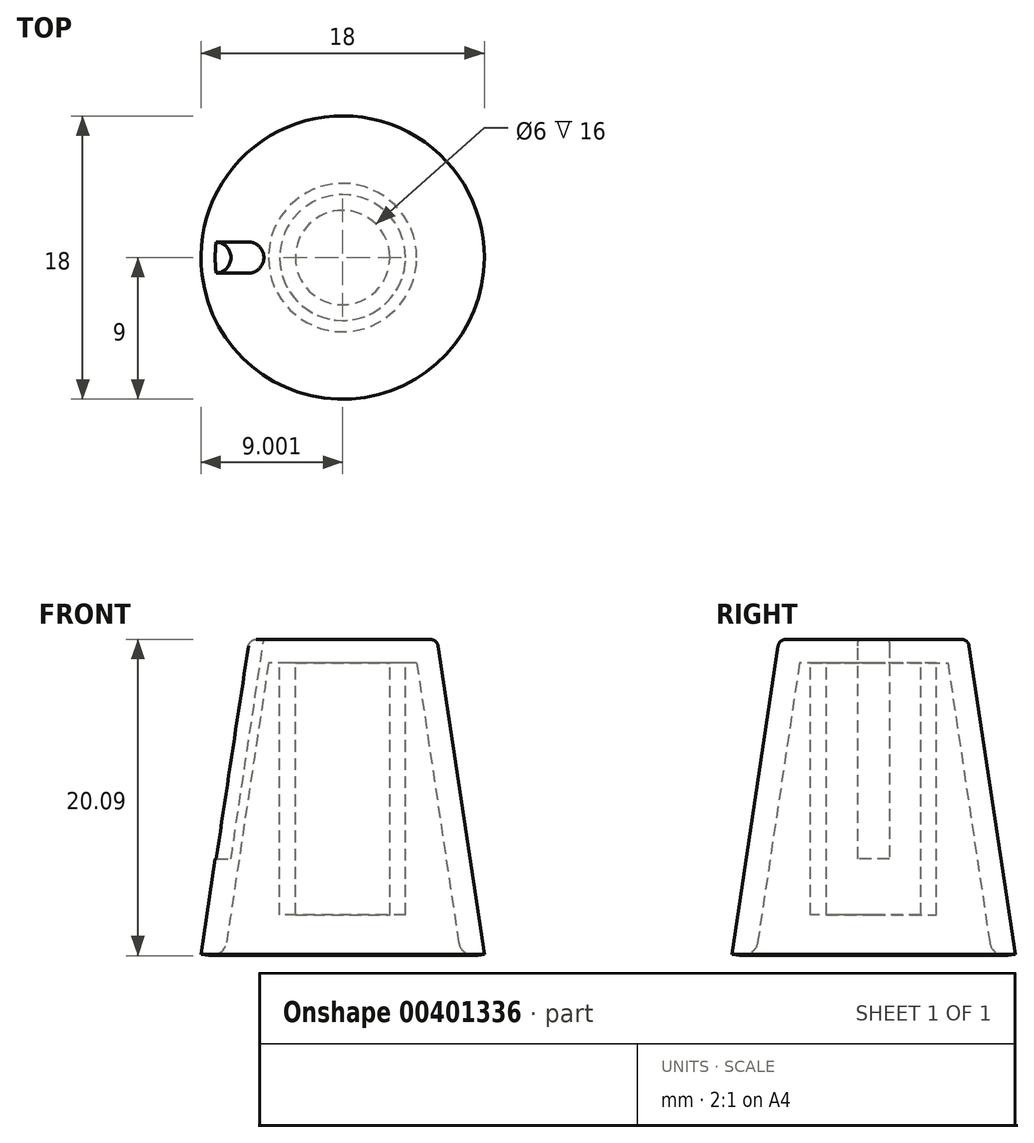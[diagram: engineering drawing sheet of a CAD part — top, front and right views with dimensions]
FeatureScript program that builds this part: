
annotation { "Feature Type Name" : "Feature", "Feature Type Description" : "" }
export const myFeature = defineFeature(function(context is Context, id is Id, definition is map)
    precondition{}
    {
        {
            var Q0;
            Q0=qCreatedBy(makeId("Front.planeOp"),FACE);
            var sketch = newSketch(context, id + "F0", { "sketchPlane" : qUnion([Q0])});
            skLineSegment(sketch, "E0", {"start": v(-12.14, 63.32) * mm, "end": v(-12.14, -77.35) * mm, "construction": true});
            skLineSegment(sketch, "E1", {"start": v(-12.14, 20) * mm, "end": v(-18.14, 20) * mm});
            skLineSegment(sketch, "E2", {"start": v(-18.14, 20) * mm, "end": v(-20.23, 6.05) * mm});
            skLineSegment(sketch, "E3.0", {"start": v(-16.85, 18.5) * mm, "end": v(-19.66, -0.22) * mm});
            skLineSegment(sketch, "E3.1", {"start": v(-12.14, 18.5) * mm, "end": v(-16.85, 18.5) * mm});
            skLineSegment(sketch, "E4", {"start": v(-21.14, 0) * mm, "end": v(-19.66, -0.22) * mm});
            skLineSegment(sketch, "E5", {"start": v(-12.14, 20) * mm, "end": v(-12.14, 18.5) * mm});
            skLineSegment(sketch, "E6", {"start": v(-20.23, 6.05) * mm, "end": v(-21.14, 0) * mm});
            skSolve(sketch);
        }
        {
            var Q0;
            Q0=makeQuery(id+"F0.imprint","IMPRINT",FACE,{"disambiguationData":[TD([[makeQuery(id+"F0.imprint","IMPRINT",EDGE,{"derivedFrom":sQuery(id+"F0.wireOp",EDGE,"E1")}),1.0]])]});
            var Q1;
            Q1=sQuery(id+"F0.wireOp",EDGE,"E0");
            revolve(context, id + "F1", {"entities" : qUnion([Q0]), "axis" : qUnion([Q1]), "revolveType" : RevolveType.FULL});
        }
        {
            var Q0;
            Q0=makeQuery(id+"F1.opRevolve","SWEPT_FACE",FACE,{"disambiguationData":[OSD([sQuery(id+"F0.wireOp",EDGE,"E1")])]});
            var sketch = newSketch(context, id + "F2", { "sketchPlane" : qUnion([Q0])});
            skCircle(sketch, "E7", {"center": v(-18.14, 0) * mm, "radius": 1 * mm});
            skSolve(sketch);
        }
        {
            var Q0;
            {var subQ0=sQuery(id+"F2.wireOp",EDGE,"E7");var subQ1=makeQuery(id+"F1.opRevolve","SWEPT_EDGE",EDGE,{"disambiguationData":[OSD([sQuery(id+"F0.wireOp",EDGE,"E1"),sQuery(id+"F0.wireOp",EDGE,"E2")])]});var subQ2=makeQuery(id+"F2.imprint","INTERSECT",VERTEX,{"disambiguationData":[OD(0.0)],"derivedFrom":[subQ1,subQ0]});Q0=makeQuery(id+"F2.imprint","IMPRINT",FACE,{"disambiguationData":[TD([[makeQuery(id+"F2.imprint","IMPRINT",EDGE,{"disambiguationData":[TD([[subQ2,-1.0]])],"derivedFrom":subQ0}),1.0]])]});}
            var Q1;
            {var subQ0=sQuery(id+"F2.wireOp",EDGE,"E7");var subQ1=makeQuery(id+"F1.opRevolve","SWEPT_EDGE",EDGE,{"disambiguationData":[OSD([sQuery(id+"F0.wireOp",EDGE,"E1"),sQuery(id+"F0.wireOp",EDGE,"E2")])]});var subQ2=makeQuery(id+"F2.imprint","INTERSECT",VERTEX,{"disambiguationData":[OD(0.0)],"derivedFrom":[subQ1,subQ0]});Q1=makeQuery(id+"F2.imprint","IMPRINT",FACE,{"disambiguationData":[TD([[makeQuery(id+"F2.imprint","IMPRINT",EDGE,{"disambiguationData":[TD([[subQ2,1.0]])],"derivedFrom":subQ0}),1.0]])]});}
            var Q2;
            Q2=sQuery(id+"F0.wireOp",EDGE,"E2");
            sweep(context, id + "F3", {"operationType" : NewBodyOperationType.REMOVE, "profiles" : qUnion([Q0, Q1]), "path" : qUnion([Q2])});
        }
        {
            var Q0;
            Q0=makeQuery(id+"F1.opRevolve","SWEPT_FACE",FACE,{"disambiguationData":[OSD([sQuery(id+"F0.wireOp",EDGE,"E3.1")])]});
            var sketch = newSketch(context, id + "F4", { "sketchPlane" : qUnion([Q0])});
            skCircle(sketch, "E8", {"center": v(-12.14, 0) * mm, "radius": 4 * mm});
            skCircle(sketch, "E9", {"center": v(-12.14, 0) * mm, "radius": 3 * mm});
            skLineSegment(sketch, "E10", {"start": v(-13.74, -2.54) * mm, "end": v(-13.74, 2.54) * mm});
            skSolve(sketch);
        }
        {
            var Q0;
            Q0=qSketchRegion(id+"F4",true);
            extrude(context, id + "F5", {"entities" : qUnion([Q0]), "operationType" : NewBodyOperationType.ADD, "depth" : 16 * mm});
        }
        {
            var Q0;
            {var subQ0=sQuery(id+"F0.wireOp",EDGE,"E1");var subQ2=sQuery(id+"F0.wireOp",EDGE,"E2");var subQ4=sQuery(id+"F2.wireOp",EDGE,"E7");var subQ5=makeQuery(id+"FBC831FxAMM4vtj_1.9.F3.opSweep","SWEPT_FACE",FACE,{"disambiguationData":[OSD([subQ2,subQ4])]});var subQ6=makeQuery(id+"F3.boolean.opBoolean","COPY",FACE,{"derivedFrom":makeQuery(id+"F3.opSweep","SWEPT_FACE",FACE,{"disambiguationData":[OSD([subQ2,subQ4])]})});Q0=makeQuery(id+"FBC831FxAMM4vtj_1.10.F3.boolean.opBoolean","SPLIT",EDGE,{"disambiguationData":[TD([makeQuery(id+"FBC831FxAMM4vtj_1.9.F3.boolean.opBoolean","COPY",FACE,{"derivedFrom":subQ5})])],"derivedFrom":makeQuery(id+"FBC831FxAMM4vtj_1.9.F3.boolean.opBoolean","SPLIT",EDGE,{"disambiguationData":[TD([subQ6])],"derivedFrom":makeQuery(id+"FBC831FxAMM4vtj_1.8.F3.boolean.opBoolean","SPLIT",EDGE,{"disambiguationData":[TD([subQ6])],"derivedFrom":makeQuery(id+"FBC831FxAMM4vtj_1.7.F3.boolean.opBoolean","SPLIT",EDGE,{"disambiguationData":[TD([subQ6])],"derivedFrom":makeQuery(id+"FBC831FxAMM4vtj_1.6.F3.boolean.opBoolean","SPLIT",EDGE,{"disambiguationData":[TD([subQ6])],"derivedFrom":makeQuery(id+"FBC831FxAMM4vtj_1.5.F3.boolean.opBoolean","SPLIT",EDGE,{"disambiguationData":[TD([subQ6])],"derivedFrom":makeQuery(id+"FBC831FxAMM4vtj_1.4.F3.boolean.opBoolean","SPLIT",EDGE,{"disambiguationData":[TD([subQ6])],"derivedFrom":makeQuery(id+"FBC831FxAMM4vtj_1.3.F3.boolean.opBoolean","SPLIT",EDGE,{"disambiguationData":[TD([subQ6])],"derivedFrom":makeQuery(id+"FBC831FxAMM4vtj_1.2.F3.boolean.opBoolean","SPLIT",EDGE,{"disambiguationData":[TD([subQ6])],"derivedFrom":makeQuery(id+"FBC831FxAMM4vtj_1.1.F3.boolean.opBoolean","SPLIT",EDGE,{"disambiguationData":[OD(0.0)],"derivedFrom":makeQuery(id+"F1.opRevolve","SWEPT_EDGE",EDGE,{"disambiguationData":[OSD([subQ0,subQ2])]})})})})})})})})})})});}
            fillet(context, id + "F6", {"entities" : qUnion([Q0]), "radius" : .5 * mm, "tangentPropagation" : true, "allowEdgeOverflow" : false});
        }
        {
            var Q0;
            Q0=makeQuery(id+"F1.opRevolve","SWEPT_EDGE",EDGE,{"disambiguationData":[OSD([sQuery(id+"F0.wireOp",EDGE,"E3.0"),sQuery(id+"F0.wireOp",EDGE,"E4")])]});
            fillet(context, id + "F7", {"entities" : qUnion([Q0]), "radius" : 1 * mm, "tangentPropagation" : true, "allowEdgeOverflow" : false});
        }
    });
